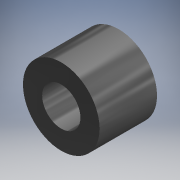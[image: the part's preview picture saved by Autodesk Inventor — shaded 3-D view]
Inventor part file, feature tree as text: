
AUTODESK INVENTOR PART (.ipt)
format: ipt  version: 2019 (Build 230136000, 136)  size: 90,112 bytes
history: native  units: mm (DEFAULTED — no unit token found)
features: extrude x1, sketch x1
ambient origin geometry x8: Origin, YZ Plane, XZ Plane, XY Plane, X Axis, Y Axis, Z Axis, Center Point
bodies: Solid1 (feature_tree)
feature tree (2):
  extrude  "Extrusion1"  Depth=3.75mm
  sketch  "Sketch1"  dims[d0=2.5mm d1=5.0mm d2=3.75mm d3=0.0mm]
